# Revit family: 203_DATL-_
name_source: partatom
category: Duct Accessories
units: mm (PartAtom-declared; Revit-internal decimal feet)

## family parameters
Always vertical = Yes
Cut with Voids When Loaded = No
Part Type = Damper
Round Connector Dimension = Use Diameter
Shared = No
Work Plane-Based = No

## types (17) — shared parameters
CAT0 = Yes
Description = CLOSING GASKETED DAMPER WITH GASKET
H1 = 50 mm  [stored 0.164042 ft]
Manufacturer = Alnor
QmdConnectorList = 201;D;202;D
URL = http://www.ventilation-alnor.co.uk
magiPartTypeId = 203
magiProductFamilyId = DATL-*

## per-type parameters (varying)
| type | D | H2D | L | L2D | LL | R | R1 | W2D |
| DATL-80 | 80 mm | 80 mm  [stored 0.262467 ft] | 85 mm  [stored 0.278871 ft] | 85 mm  [stored 0.278871 ft] | 43 mm | 40 mm  [stored 0.131234 ft] | 26 mm | 80 mm  [stored 0.262467 ft] |
| DATL-630 | 630 mm | 630 mm | 140 mm | 140 mm | 70 mm | 315 mm | 42 mm | 630 mm |
| DATL-600 | 600 mm | 600 mm | 140 mm | 140 mm | 70 mm | 300 mm | 42 mm | 600 mm |
| DATL-560 | 560 mm | 560 mm | 140 mm | 140 mm | 70 mm | 280 mm | 42 mm | 560 mm |
| DATL-500 | 500 mm | 500 mm | 140 mm | 140 mm | 70 mm | 250 mm | 42 mm | 500 mm |
| DATL-450 | 450 mm | 450 mm | 140 mm | 140 mm | 70 mm | 225 mm | 42 mm | 450 mm |
| DATL-400 | 400 mm | 400 mm | 140 mm | 140 mm | 70 mm | 200 mm | 42 mm | 400 mm |
| DATL-355 | 355 mm | 355 mm | 140 mm | 140 mm | 70 mm | 178 mm | 42 mm | 355 mm |
| DATL-315 | 315 mm | 315 mm | 85 mm  [stored 0.278871 ft] | 85 mm  [stored 0.278871 ft] | 43 mm | 158 mm | 26 mm | 315 mm |
| DATL-250 | 250 mm | 250 mm | 85 mm  [stored 0.278871 ft] | 85 mm  [stored 0.278871 ft] | 43 mm | 125 mm | 26 mm | 250 mm |
| DATL-224 | 220 mm | 224 mm | 85 mm  [stored 0.278871 ft] | 85 mm  [stored 0.278871 ft] | 43 mm | 110 mm | 26 mm | 224 mm |
| DATL-200 | 200 mm | 200 mm | 85 mm  [stored 0.278871 ft] | 85 mm  [stored 0.278871 ft] | 43 mm | 100 mm  [stored 0.328084 ft] | 26 mm | 200 mm |
| DATL-180 | 180 mm | 180 mm | 85 mm  [stored 0.278871 ft] | 85 mm  [stored 0.278871 ft] | 43 mm | 90 mm | 26 mm | 180 mm |
| DATL-160 | 160 mm | 160 mm | 85 mm  [stored 0.278871 ft] | 85 mm  [stored 0.278871 ft] | 43 mm | 80 mm  [stored 0.262467 ft] | 26 mm | 160 mm |
| DATL-150 | 150 mm | 150 mm | 85 mm  [stored 0.278871 ft] | 85 mm  [stored 0.278871 ft] | 43 mm | 75 mm | 26 mm | 150 mm |
| DATL-125 | 125 mm | 125 mm | 85 mm  [stored 0.278871 ft] | 85 mm  [stored 0.278871 ft] | 43 mm | 63 mm | 26 mm | 125 mm |
| DATL-100 | 100 mm | 100 mm  [stored 0.328084 ft] | 85 mm  [stored 0.278871 ft] | 85 mm  [stored 0.278871 ft] | 43 mm | 50 mm  [stored 0.164042 ft] | 26 mm | 100 mm  [stored 0.328084 ft] |

note: column(s) folded — value = type name in every type: MC Product Code, magiProductId

note: [stored X ft] marks values corroborated as IEEE doubles in the binary element streams (Revit-internal decimal feet)

## geometry (parser evidence)
native form markers: Blend x4, Sweep x2
no freeform markers — native parametric forms only
